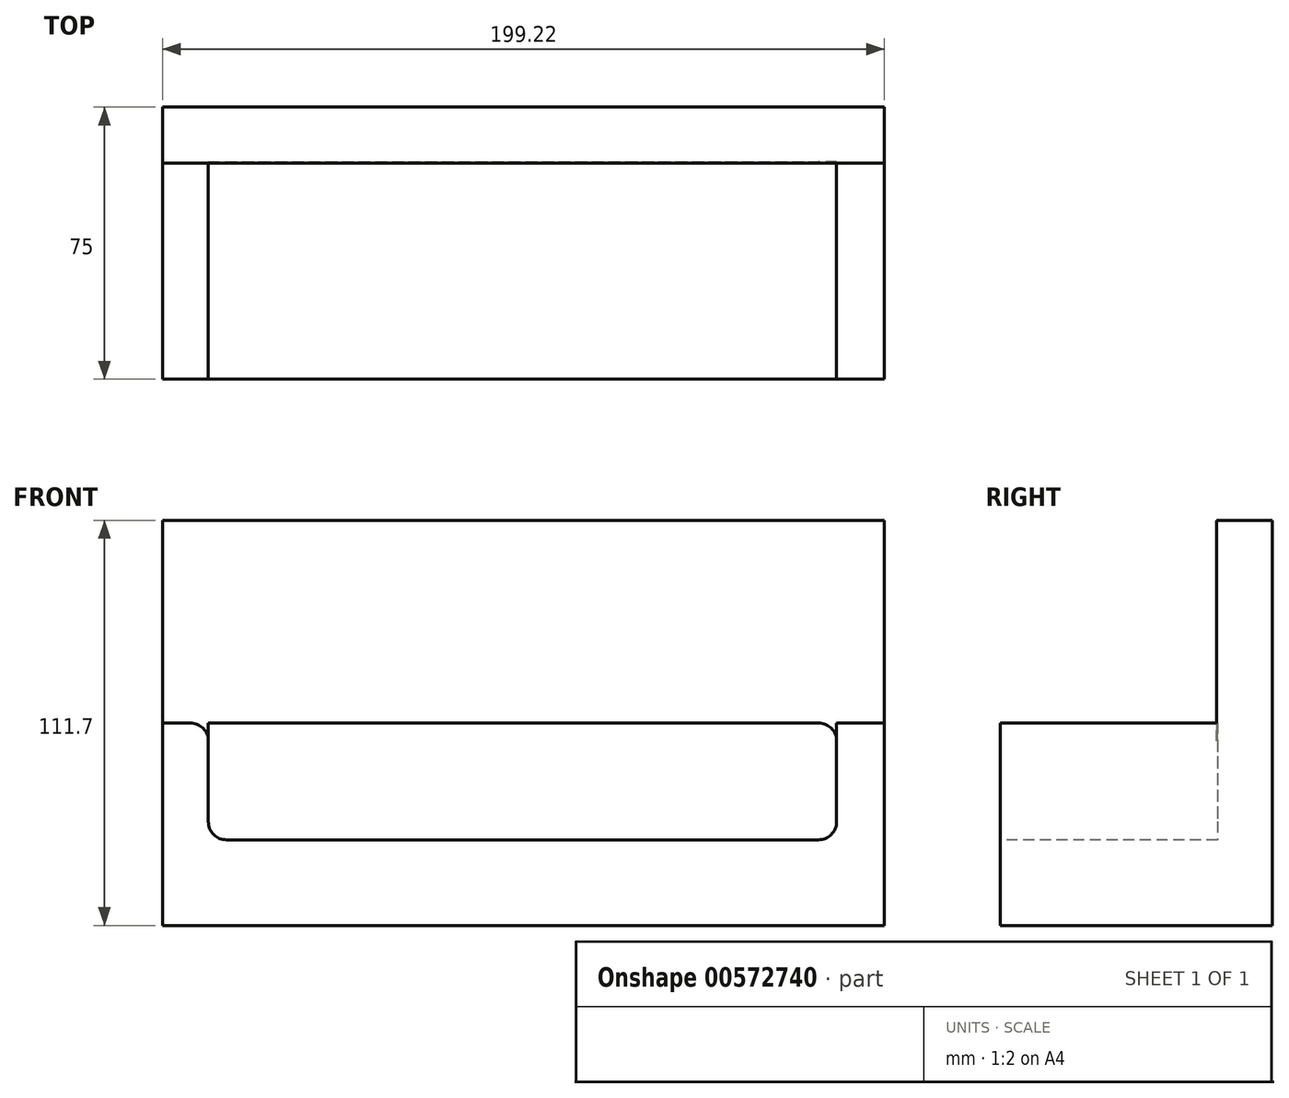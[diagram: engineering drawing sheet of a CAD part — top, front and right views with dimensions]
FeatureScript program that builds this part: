
annotation { "Feature Type Name" : "Feature", "Feature Type Description" : "" }
export const myFeature = defineFeature(function(context is Context, id is Id, definition is map)
    precondition{}
    {
        {
            var Q0;
            Q0=qCreatedBy(makeId("Front.planeOp"),FACE);
            var sketch = newSketch(context, id + "F0", { "sketchPlane" : qUnion([Q0])});
            skLineSegment(sketch, "E0.bottom", {"start": v(99.6, 55.85) * mm, "end": v(-99.6, 55.85) * mm});
            skLineSegment(sketch, "E0.top", {"start": v(99.6, -55.85) * mm, "end": v(-99.6, -55.85) * mm});
            skLineSegment(sketch, "E0.left", {"start": v(99.6, 55.85) * mm, "end": v(99.6, -55.85) * mm});
            skLineSegment(sketch, "E0.right", {"start": v(-99.6, 55.85) * mm, "end": v(-99.6, -55.85) * mm});
            skPoint(sketch, "E0.middle", {"position": v(0, 0) * mm});
            skSolve(sketch);
        }
        {
            var Q0;
            Q0=makeQuery(id+"F0.imprint","IMPRINT",FACE,{"disambiguationData":[TD([[makeQuery(id+"F0.imprint","IMPRINT",EDGE,{"derivedFrom":sQuery(id+"F0.wireOp",EDGE,"E0.bottom")}),1.0]])]});
            extrude(context, id + "F1", {"entities" : qUnion([Q0]), "depth" : 75 * mm, "offsetDistance" : 25 * mm});
        }
        {
            var Q0;
            Q0=makeQuery(id+"F1.opExtrude","CAP_FACE",FACE,{"disambiguationData":[OSD([sQuery(id+"F0.wireOp",EDGE,"E0.bottom"),sQuery(id+"F0.wireOp",EDGE,"E0.top"),sQuery(id+"F0.wireOp",EDGE,"E0.left"),sQuery(id+"F0.wireOp",EDGE,"E0.right")])],"isStart":false});
            var sketch = newSketch(context, id + "F2", { "sketchPlane" : qUnion([Q0])});
            skPoint(sketch, "E1.oppositeSnap0", {"position": v(99.6, 0) * mm});
            skLineSegment(sketch, "E1.bottom", {"start": v(-99.6, 55.85) * mm, "end": v(100.22, 55.85) * mm});
            skLineSegment(sketch, "E1.top", {"start": v(-99.6, 0) * mm, "end": v(100.22, 0) * mm});
            skLineSegment(sketch, "E1.left", {"start": v(-99.6, 55.85) * mm, "end": v(-99.6, 0) * mm});
            skLineSegment(sketch, "E1.right", {"start": v(100.22, 55.85) * mm, "end": v(100.22, 0) * mm});
            skSolve(sketch);
        }
        {
            var Q0;
            {var subQ3=sQuery(id+"F2.wireOp",EDGE,"E1.left");Q0=makeQuery(id+"F2.imprint","IMPRINT",FACE,{"disambiguationData":[TD([[makeQuery(id+"F2.imprint","IMPRINT",EDGE,{"derivedFrom":subQ3}),1.0]])]});}
            extrude(context, id + "F3", {"entities" : qUnion([Q0]), "operationType" : NewBodyOperationType.REMOVE, "oppositeDirection" : true, "depth" : 59.6 * mm, "offsetDistance" : 25 * mm});
        }
        {
            var Q0;
            Q0=makeQuery(id+"F1.opExtrude","CAP_FACE",FACE,{"disambiguationData":[OSD([sQuery(id+"F0.wireOp",EDGE,"E0.bottom"),sQuery(id+"F0.wireOp",EDGE,"E0.top"),sQuery(id+"F0.wireOp",EDGE,"E0.left"),sQuery(id+"F0.wireOp",EDGE,"E0.right")])],"isStart":false});
            var sketch = newSketch(context, id + "F4", { "sketchPlane" : qUnion([Q0])});
            skLineSegment(sketch, "E2.bottom", {"start": v(-86.94, 0) * mm, "end": v(86.41, 0) * mm});
            skLineSegment(sketch, "E2.top", {"start": v(-86.94, -32.24) * mm, "end": v(86.41, -32.24) * mm});
            skLineSegment(sketch, "E2.left", {"start": v(-86.94, 0) * mm, "end": v(-86.94, -32.24) * mm});
            skLineSegment(sketch, "E2.right", {"start": v(86.41, 0) * mm, "end": v(86.41, -32.24) * mm});
            skSolve(sketch);
        }
        {
            var Q0;
            Q0=makeQuery(id+"F4.imprint","IMPRINT",FACE,{"disambiguationData":[TD([[makeQuery(id+"F4.imprint","IMPRINT",EDGE,{"derivedFrom":sQuery(id+"F4.wireOp",EDGE,"E2.bottom")}),-1.0]])]});
            extrude(context, id + "F5", {"entities" : qUnion([Q0]), "operationType" : NewBodyOperationType.REMOVE, "oppositeDirection" : true, "depth" : 59.9 * mm, "offsetDistance" : 25 * mm});
        }
        {
            var Q0;
            Q0=makeQuery(id+"F3.boolean.opBoolean","COPY",EDGE,{"derivedFrom":makeQuery(id+"F3.opExtrude","SWEPT_EDGE",EDGE,{"disambiguationData":[OSD([sQuery(id+"F0.wireOp",EDGE,"E0.right"),sQuery(id+"F2.wireOp",EDGE,"E1.top"),sQuery(id+"F2.wireOp",EDGE,"E1.left")])]})});
            var Q1;
            {var subQ0=sQuery(id+"F2.wireOp",EDGE,"E1.top");var subQ1=sQuery(id+"F4.wireOp",EDGE,"E2.left");Q1=makeQuery(id+"F5.boolean.opBoolean","COPY",EDGE,{"disambiguationData":[topologyDisambiguationEdgeConnected([makeQuery(id+"F3.boolean.opBoolean","COPY",FACE,{"derivedFrom":makeQuery(id+"F3.opExtrude","SWEPT_FACE",FACE,{"disambiguationData":[OSD([subQ0])]})})])],"derivedFrom":makeQuery(id+"F5.opExtrude","SWEPT_EDGE",EDGE,{"disambiguationData":[OSD([subQ0,sQuery(id+"F4.wireOp",EDGE,"E2.bottom"),subQ1])]})});}
            var Q2;
            Q2=makeQuery(id+"F5.boolean.opBoolean","COPY",EDGE,{"derivedFrom":makeQuery(id+"F5.opExtrude","SWEPT_EDGE",EDGE,{"disambiguationData":[OSD([sQuery(id+"F4.wireOp",EDGE,"E2.top"),sQuery(id+"F4.wireOp",EDGE,"E2.left")])]})});
            var Q3;
            Q3=makeQuery(id+"F5.boolean.opBoolean","COPY",EDGE,{"derivedFrom":makeQuery(id+"F5.opExtrude","SWEPT_EDGE",EDGE,{"disambiguationData":[OSD([sQuery(id+"F4.wireOp",EDGE,"E2.top"),sQuery(id+"F4.wireOp",EDGE,"E2.right")])]})});
            var Q4;
            {var subQ0=sQuery(id+"F2.wireOp",EDGE,"E1.top");var subQ1=sQuery(id+"F4.wireOp",EDGE,"E2.right");Q4=makeQuery(id+"F5.boolean.opBoolean","COPY",EDGE,{"disambiguationData":[topologyDisambiguationEdgeConnected([makeQuery(id+"F3.boolean.opBoolean","COPY",FACE,{"derivedFrom":makeQuery(id+"F3.opExtrude","SWEPT_FACE",FACE,{"disambiguationData":[OSD([subQ0])]})})])],"derivedFrom":makeQuery(id+"F5.opExtrude","SWEPT_EDGE",EDGE,{"disambiguationData":[OSD([subQ0,sQuery(id+"F4.wireOp",EDGE,"E2.bottom"),subQ1])]})});}
            var Q5;
            Q5=makeQuery(id+"F3.boolean.opBoolean","COPY",EDGE,{"derivedFrom":makeQuery(id+"F3.opExtrude","SWEPT_EDGE",EDGE,{"disambiguationData":[OSD([sQuery(id+"F0.wireOp",EDGE,"E0.left"),sQuery(id+"F2.wireOp",EDGE,"E1.top")])]})});
            var Q6;
            Q6=makeQuery(id+"F3.boolean.opBoolean","COPY",EDGE,{"derivedFrom":makeQuery(id+"F3.opExtrude","CAP_EDGE",EDGE,{"disambiguationData":[OSD([sQuery(id+"F2.wireOp",EDGE,"E1.left")])],"isStart":false})});
            var Q7;
            Q7=makeQuery(id+"F3.boolean.opBoolean","COPY",EDGE,{"derivedFrom":makeQuery(id+"F3.opExtrude","CAP_EDGE",EDGE,{"disambiguationData":[OSD([sQuery(id+"F2.wireOp",EDGE,"E1.bottom")])],"isStart":false})});
            var Q8;
            Q8=makeQuery(id+"F3.boolean.opBoolean","COPY",EDGE,{"derivedFrom":makeQuery(id+"F3.opExtrude","CAP_EDGE",EDGE,{"disambiguationData":[OSD([sQuery(id+"F0.wireOp",EDGE,"E0.left")])],"isStart":false})});
            fillet(context, id + "F6", {"entities" : qUnion([Q0, Q1, Q2, Q3, Q4, Q5, Q6, Q7, Q8]), "radius" : 5 * mm, "tangentPropagation" : true, "allowEdgeOverflow" : false});
        }
    });
